# Revit family: IS_Connect_E8101_BIM_DE
name_source: partatom
category: Plumbing Fixtures
revit_build: Autodesk Revit MEP 2016 (Build: 20161004_0715(x64)
units: mm (PartAtom-declared; Revit-internal decimal feet)

## family parameters
Always vertical = No
Cut with Voids When Loaded = No
OmniClass Number = 23.45.05.14.14
OmniClass Title = Sinks/Lavatories
Part Type = Normal
Room Calculation Point = No
Round Connector Dimension = Use Diameter
Shared = No
Work Plane-Based = No

## types (2) — shared parameters
Accessories = www.idealstandard.de\ersatzteile
AreaUnits = millimeters
AssetType = Fixed
BIMobject category = Basins
BOSUseNativeGeometries = 1
Brand = Ideal Standard
Brand url = http://www.idealstandard.de
CodePerformance = DIN EN 14688 CL 10, DIN EN 31
ConnectionType = Plumbing
CurrencyUnit = €
DurationUnit = year
Edition number = 1
ExpectedLife = 25
Features = CONNECT CUBE washbasin 600x460mm, no taphole, with overflow
IFC Classification = Sanitary Terminal
IfcExportAs = WASHHANDBASIN
IfcExportType = Sanitary Terminal
Installation instructions = http://www.idealstandard.de
InstallationInstructions = www.idealstandard.de\produkte
LinearUnits = millimeters
Manufacturer name = Ideal Standard
ManufacturerURL = http://www.idealstandard.de
Material = Vitreous china
Material main = Ceramics
NBS Reference Code = 35-79-94
NBS Reference Description = Wall-Hung Wash Basins
NettWeight = 17,502 kg
Nominal height = 175
Nominal width = 600
NominalDepth = 460 mm  [stored 1.50919 ft]
NominalHeight = 174 mm
NominalLength = 460 mm  [stored 1.50919 ft]
NominalWidth = 600 mm  [stored 1.9685 ft]
OmniClass Code = 23-31 13 00
OmniClass Description = Sinks
Product Guid = 118deecb-807f-4372-927e-074483212195
Product SKU = E8101
Product certification = DIN EN 14688 CL 10, DIN EN 31
Product data url = https://bimobject.com
Product family = CONNECT
Product group = Basin
Product name = CONNECT CUBE washbasin 600x460mm, no taphole, with overflow
Product url = http://www.idealstandard.de
ProductInformation = http://www.idealstandard.de
QR code = http://bimobject.com
Shape = Sculptured
Size = 174 x 460 x 600mm
Space = Internal
SpareParts = www.idealstandard.de/ersatzteile
Technical description = http://www.idealstandard.de
Uniclass 1.4 Code = L7212
Uniclass 1.4 Description = Washbasins
Uniclass 2.0 Code = PR-35-79-94
Uniclass 2.0 Description = Wall-Hung Wash Basins
Uniclass 2015 Code = Pr_40_20_96_96
Uniclass 2015 Name = Wall-hung wash basins
Uniclass2015Code = Pr_40_20_96_96
Uniclass2015Title = Wall-hung wash basins
Uniclass2015Version = Products v1.1
Version = 1
VolumeUnits = Litres
WashHandBasinMounting = WallHung
WashHandBasinType = HANDRINSE
Weight Net (Kg) = 17.5
zero-valued in all types: DrainSize

## per-type parameters (varying)
| type | BarCode | Color | Description | EAN code | Finish | MainColor | Model | ModelNumber | ModelReference |
| E810101 - CONNECT CUBE washbasin 600x460mm, no taphole, with overflow | 5017830403777 | White | E810101 CONNECT CUBE washbasin 600x460mm, no taphole, with overflow | https://5017830403777 | White | White | E810101 | E810101 | E810101 CONNECT CUBE washbasin 600x460mm, no taphole, with overflow |
| E8101MA - CONNECT CUBE washbasin 600x460mm, no taphole, with overflow | 5017830403760 | WHITE IP | E8101MA CONNECT CUBE washbasin 600x460mm, no taphole, with overflow | https://5017830403760 | WHITE IP | WHITE IP | E8101MA | E8101MA | E8101MA CONNECT CUBE washbasin 600x460mm, no taphole, with overflow |

note: [stored X ft] marks values corroborated as IEEE doubles in the binary element streams (Revit-internal decimal feet)

## geometry (parser evidence)
native form markers: Blend x2, Sweep x3
no freeform markers — native parametric forms only
